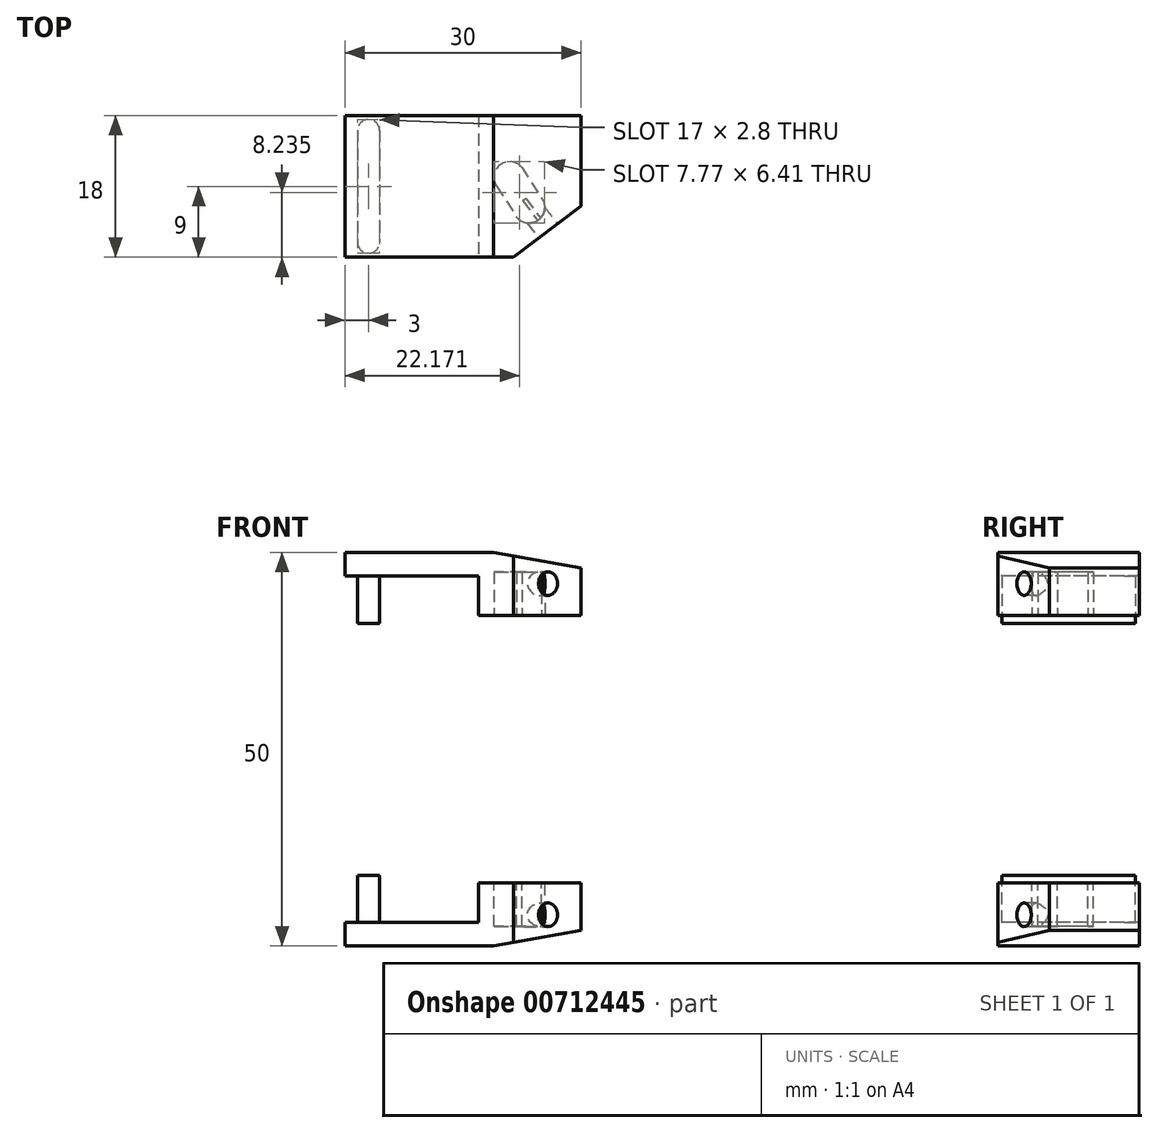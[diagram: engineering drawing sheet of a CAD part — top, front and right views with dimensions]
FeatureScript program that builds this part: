
annotation { "Feature Type Name" : "Feature", "Feature Type Description" : "" }
export const myFeature = defineFeature(function(context is Context, id is Id, definition is map)
    precondition{}
    {
        {
            var Q0;
            Q0=qCreatedBy(makeId("Top.planeOp"),FACE);
            var sketch = newSketch(context, id + "F0", { "sketchPlane" : qUnion([Q0])});
            skLineSegment(sketch, "E0.bottom", {"start": v(0, 0) * mm, "end": v(30, 0) * mm});
            skLineSegment(sketch, "E0.top", {"start": v(0, -18) * mm, "end": v(30, -18) * mm});
            skLineSegment(sketch, "E0.left", {"start": v(0, 0) * mm, "end": v(0, -18) * mm});
            skLineSegment(sketch, "E0.right", {"start": v(30, 0) * mm, "end": v(30, -18) * mm});
            skSolve(sketch);
        }
        {
            var Q0;
            Q0 = qSketchRegion(id + "F0", true);
            extrude(context, id + "F1", {"entities" : qUnion([Q0]), "depth" : 9 * mm, "offsetDistance" : 25 * mm});
        }
        {
            var Q0;
            Q0=makeQuery(id+"F1.opExtrude","CAP_FACE",FACE,{"disambiguationData":[OSD([sQuery(id+"F0.wireOp",EDGE,"E0.bottom"),sQuery(id+"F0.wireOp",EDGE,"E0.top"),sQuery(id+"F0.wireOp",EDGE,"E0.left"),sQuery(id+"F0.wireOp",EDGE,"E0.right")])],"isStart":false});
            var sketch = newSketch(context, id + "F2", { "sketchPlane" : qUnion([Q0])});
            skCircle(sketch, "E1", {"center": v(3, -1.9) * mm, "radius": 1.4 * mm});
            skCircle(sketch, "E2", {"center": v(3, -16.1) * mm, "radius": 1.4 * mm});
            skLineSegment(sketch, "E3", {"start": v(1.6, -1.9) * mm, "end": v(1.6, -16.1) * mm});
            skLineSegment(sketch, "E4", {"start": v(4.4, -1.9) * mm, "end": v(4.4, -16.1) * mm});
            skSolve(sketch);
        }
        {
            var Q0;
            {var subQ0=sQuery(id+"F2.wireOp",EDGE,"E3");Q0=makeQuery(id+"F2.imprint","IMPRINT",FACE,{"disambiguationData":[TD([[makeQuery(id+"F2.imprint","IMPRINT",EDGE,{"derivedFrom":subQ0}),-1.0]])]});}
            extrude(context, id + "F3", {"entities" : qUnion([Q0]), "operationType" : NewBodyOperationType.REMOVE, "oppositeDirection" : true, "depth" : 6 * mm, "offsetDistance" : 25 * mm});
        }
        {
            var Q0;
            Q0=makeQuery(id+"F3.boolean.opBoolean","COPY",FACE,{"derivedFrom":makeQuery(id+"F3.opExtrude","CAP_FACE",FACE,{"disambiguationData":[OSD([sQuery(id+"F0.wireOp",EDGE,"E0.bottom"),sQuery(id+"F0.wireOp",EDGE,"E0.top"),sQuery(id+"F0.wireOp",EDGE,"E0.left"),sQuery(id+"F0.wireOp",EDGE,"E0.right"),sQuery(id+"F2.wireOp",EDGE,"E1"),sQuery(id+"F2.wireOp",EDGE,"E2"),sQuery(id+"F2.wireOp",EDGE,"E3"),sQuery(id+"F2.wireOp",EDGE,"E4")])],"isStart":false})});
            var sketch = newSketch(context, id + "F4", { "sketchPlane" : qUnion([Q0])});
            skLineSegment(sketch, "E5", {"start": v(21.42, -18) * mm, "end": v(30, -11.48) * mm});
            skLineSegment(sketch, "E6", {"start": v(30, -11.48) * mm, "end": v(30, -18) * mm});
            skLineSegment(sketch, "E7", {"start": v(30, -18) * mm, "end": v(21.42, -18) * mm});
            skSolve(sketch);
        }
        {
            var Q0;
            Q0 = qSketchRegion(id + "F4", true);
            extrude(context, id + "F5", {"entities" : qUnion([Q0]), "operationType" : NewBodyOperationType.REMOVE, "oppositeDirection" : true, "depth" : 25 * mm, "offsetDistance" : 25 * mm});
        }
        {
            var Q0;
            Q0=makeQuery(id+"F3.boolean.opBoolean","COPY",FACE,{"derivedFrom":makeQuery(id+"F3.opExtrude","CAP_FACE",FACE,{"disambiguationData":[OSD([sQuery(id+"F0.wireOp",EDGE,"E0.bottom"),sQuery(id+"F0.wireOp",EDGE,"E0.top"),sQuery(id+"F0.wireOp",EDGE,"E0.left"),sQuery(id+"F0.wireOp",EDGE,"E0.right"),sQuery(id+"F2.wireOp",EDGE,"E1"),sQuery(id+"F2.wireOp",EDGE,"E2"),sQuery(id+"F2.wireOp",EDGE,"E3"),sQuery(id+"F2.wireOp",EDGE,"E4")])],"isStart":false})});
            var sketch = newSketch(context, id + "F6", { "sketchPlane" : qUnion([Q0])});
            skLineSegment(sketch, "E8.bottom", {"start": v(30, 0) * mm, "end": v(17, 0) * mm});
            skLineSegment(sketch, "E8.left", {"start": v(30, 0) * mm, "end": v(30, -11.48) * mm});
            skLineSegment(sketch, "E8.right", {"start": v(17, 0) * mm, "end": v(17, -11.48) * mm});
            skLineSegment(sketch, "E9", {"start": v(17, -11.48) * mm, "end": v(17, -18) * mm});
            skLineSegment(sketch, "E10", {"start": v(17, -18) * mm, "end": v(21.42, -18) * mm});
            skLineSegment(sketch, "E11", {"start": v(21.42, -18) * mm, "end": v(30, -11.48) * mm});
            skSolve(sketch);
        }
        {
            var Q0;
            Q0 = qSketchRegion(id + "F6", true);
            extrude(context, id + "F7", {"entities" : qUnion([Q0]), "operationType" : NewBodyOperationType.ADD, "depth" : 5 * mm, "offsetDistance" : 25 * mm});
        }
        {
            var Q0;
            Q0=makeQuery(id+"F7.boolean.opBoolean","MERGE",FACE,{"derivedFrom":[makeQuery(id+"F5.boolean.opBoolean","COPY",FACE,{"derivedFrom":makeQuery(id+"F5.opExtrude","SWEPT_FACE",FACE,{"disambiguationData":[OSD([sQuery(id+"F4.wireOp",EDGE,"E5")])]})}),makeQuery(id+"F7.opExtrude","SWEPT_FACE",FACE,{"disambiguationData":[OSD([sQuery(id+"F6.wireOp",EDGE,"E11")])]})]});
            var sketch = newSketch(context, id + "F8", { "sketchPlane" : qUnion([Q0])});
            skCircle(sketch, "E12", {"center": v(11.66, 3.96) * mm, "radius": 1.5 * mm});
            skSolve(sketch);
        }
        {
            var Q0;
            Q0 = qSketchRegion(id + "F8", true);
            extrude(context, id + "F9", {"entities" : qUnion([Q0]), "operationType" : NewBodyOperationType.REMOVE, "oppositeDirection" : true, "depth" : 5 * mm, "offsetDistance" : 25 * mm});
        }
        {
            var Q0;
            Q0=makeQuery(id+"F7.opExtrude","CAP_FACE",FACE,{"disambiguationData":[OSD([sQuery(id+"F6.wireOp",EDGE,"E8.bottom"),sQuery(id+"F6.wireOp",EDGE,"E8.left"),sQuery(id+"F6.wireOp",EDGE,"E8.right"),sQuery(id+"F6.wireOp",EDGE,"E9"),sQuery(id+"F6.wireOp",EDGE,"E10"),sQuery(id+"F6.wireOp",EDGE,"E11")])],"isStart":false});
            var sketch = newSketch(context, id + "F10", { "sketchPlane" : qUnion([Q0])});
            skArc(sketch, "E13", {"start": v(21.81, -12.9) * mm, "mid": v(24.62, -13.25) * mm, "end": v(24.97, -10.44) * mm});
            skLineSegment(sketch, "E14", {"start": v(22.47, -6.58) * mm, "end": v(24.97, -10.44) * mm});
            skLineSegment(sketch, "E15", {"start": v(19.25, -8.95) * mm, "end": v(21.81, -12.9) * mm});
            skArc(sketch, "E16", {"start": v(22.47, -6.58) * mm, "mid": v(19.74, -6.26) * mm, "end": v(19.25, -8.95) * mm});
            skSolve(sketch);
        }
        {
            var Q0;
            Q0 = qSketchRegion(id + "F10", true);
            extrude(context, id + "F11", {"entities" : qUnion([Q0]), "operationType" : NewBodyOperationType.REMOVE, "oppositeDirection" : true, "depth" : 5.52 * mm, "offsetDistance" : 25 * mm});
        }
        {
            var Q0;
            Q0=makeQuery(id+"F7.boolean.opBoolean","MERGE",FACE,{"derivedFrom":[makeQuery(id+"F1.opExtrude","SWEPT_FACE",FACE,{"disambiguationData":[OSD([sQuery(id+"F0.wireOp",EDGE,"E0.bottom")])]}),makeQuery(id+"F7.opExtrude","SWEPT_FACE",FACE,{"disambiguationData":[OSD([sQuery(id+"F6.wireOp",EDGE,"E8.bottom")])]})]});
            var sketch = newSketch(context, id + "F12", { "sketchPlane" : qUnion([Q0])});
            skLineSegment(sketch, "E17", {"start": v(-30, 1.97) * mm, "end": v(-18.89, 0) * mm});
            skLineSegment(sketch, "E18", {"start": v(-18.89, 0) * mm, "end": v(-30, 0) * mm});
            skLineSegment(sketch, "E19", {"start": v(-30, 0) * mm, "end": v(-30, 1.97) * mm});
            skSolve(sketch);
        }
        {
            var Q0;
            Q0 = qSketchRegion(id + "F12", true);
            extrude(context, id + "F13", {"entities" : qUnion([Q0]), "operationType" : NewBodyOperationType.REMOVE, "oppositeDirection" : true, "depth" : 25 * mm, "offsetDistance" : 25 * mm});
        }
        {
            var Q0;
            Q0=qCreatedBy(makeId("Top.planeOp"),FACE);
            cPlane(context, id + "F14", {"entities" : qUnion([Q0]), "cplaneType" : CPlaneType.OFFSET, "offset" : 25 * mm, "width" : 150 * mm, "height" : 150 * mm});
        }
        {
            var Q0;
            Q0=makeQuery(id+"F1.opExtrude","SWEPT_BODY",BODY,{"disambiguationData":[OSD([sQuery(id+"F0.wireOp",EDGE,"E0.bottom"),sQuery(id+"F0.wireOp",EDGE,"E0.top"),sQuery(id+"F0.wireOp",EDGE,"E0.left"),sQuery(id+"F0.wireOp",EDGE,"E0.right")])]});
            var Q1;
            Q1=qCreatedBy(id+"F14.planeOp",FACE);
            mirror(context, id + "F15", {"entities" : qUnion([Q0]), "mirrorPlane" : qUnion([Q1])});
        }
    });
